# Revit family: STH20964PTO_27
name_source: partatom
category: Luminárias
units: mm (PartAtom-declared; Revit-internal decimal feet)

## family parameters
Compartilhado = Não
Corte com vazios quando carregada = Não
Cota do conector redondo = Utilizar diâmetro
Fonte luminosa = Não
Hospedeiro = Forro
Manter orientação da anotação = Não
Número OmniClass = 23.80.70.11
Ponto de cálculo do ambiente = Não
Sempre na vertical = Sim
Tipo de parte = Normal
Título OmniClass = Luminaries for Internal Lighting

## types (1)
- STH20964PTO/27 - PRETO - 2m - 2700K - 700lm - 90°
    Altura = 0.03 m
    Comprimento = 2.01 m
    Dimerização = Não dimerizável
    Elevação padrão = 0 m
    Estrutura = Al - Preto
    Fabricante = Stella
    Fluxo Luminoso = 700 lm
    Grau de proteção (IP) = IP20
    IRC (Índice de reprodução de cores) = >93 (R9 >60)
    Largura = 0.03 m
    Luminoso = Luminoso_Lente Preta - 2700K
    Modelo = Archi
    Potência = 19 W
    Referência = STH20964PTO/27 - PRETO - 2m
    Temperatura da cor (K) = 2700 K
    Tensão Elétrica = 24V
    URL = https://stella.com.br
    Ângulo de Abertura = 90°
